# Revit family: Panel Aislante i16
name_source: partatom
category: Generic Models
revit_build: Autodesk Revit 2016 (Build: 20150220_1215(x64)
units: mm (PartAtom-declared; Revit-internal decimal feet)

## family parameters
Can host rebar = No
Cut with Voids When Loaded = No
Host = Face
Part Type = Normal
Room Calculation Point = No
Round Connector Dimension = Use Diameter
Shared = No

## types (8) — shared parameters
Adsorción de humedad (Peso) = 0.43%
Adsorción de humedad (Volumen) = 0.0071%
Ancho = 60 cm
Conductividad Termica = 0.0316W/m.K
Default Elevation = 122 cm
Densidad Aparente = 17.2kg/m3
Manufacturer = NOVIDESA
Model = IKOS i16
Permeabilidad al vapor de agua = 0.046 ng/Pa.s.m
URL = www.novidesa.com.mx

## per-type parameters (varying)
| type | Ailamiento termico (M) m2.K/W | Ailamiento termico (R) h.ft2.°F/BTU | Espesor | Poste Ancho |
| IKOS 6 | 1.89 | 10.77 | 6 cm | 6 cm |
| IKOS 8 | 2.41 | 13.70 | 8 cm | 6 cm |
| IKOS 10-a | 2.87 | 16.34 | 10 cm | 8 cm |
| IKOS 10-b | 2.92 | 16.60 | 10 cm | 10 cm |
| IKOS 12-a | 3.39 | 19.29 | 12 cm | 10 cm |
| IKOS 12-b | 3.16 | 17.99 | 12 cm | 12 cm |
| IKOS 15 | 3.39 | 22.33 | 15 cm | 12 cm |
| IKOS 20 | 3.86 | 21.98 | 20 cm | 12 cm |

## geometry (parser evidence)
native form markers: Sweep x2
no freeform markers — native parametric forms only
